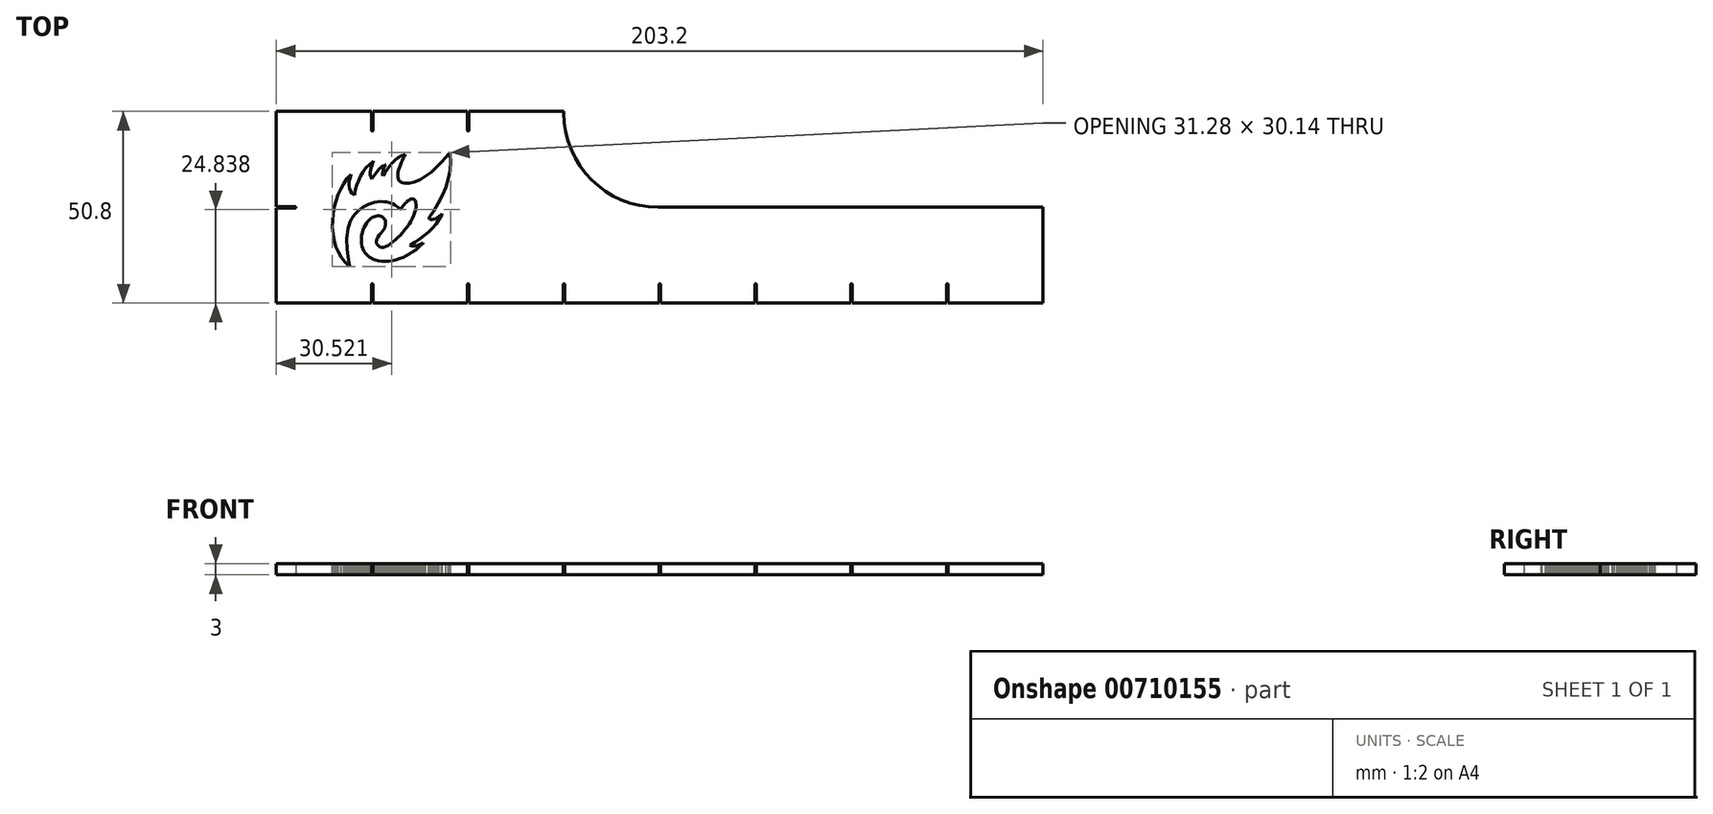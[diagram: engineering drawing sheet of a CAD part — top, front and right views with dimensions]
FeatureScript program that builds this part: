
annotation { "Feature Type Name" : "Feature", "Feature Type Description" : "" }
export const myFeature = defineFeature(function(context is Context, id is Id, definition is map)
    precondition{}
    {
        {
            var Q0;
            Q0=qCreatedBy(makeId("Top.planeOp"),FACE);
            var sketch = newSketch(context, id + "F0", { "sketchPlane" : qUnion([Q0])});
            skLineSegment(sketch, "E0", {"start": v(-76.2, 0) * mm, "end": v(127, 0) * mm});
            skLineSegment(sketch, "E1", {"start": v(127, 0) * mm, "end": v(127, 25.4) * mm});
            skLineSegment(sketch, "E2", {"start": v(127, 25.4) * mm, "end": v(0, 25.4) * mm});
            skLineSegment(sketch, "E3", {"start": v(0, 25.4) * mm, "end": v(0, 50.8) * mm});
            skLineSegment(sketch, "E4", {"start": v(0, 50.8) * mm, "end": v(-76.2, 50.8) * mm});
            skLineSegment(sketch, "E5", {"start": v(-76.2, 50.8) * mm, "end": v(-76.2, 0) * mm});
            skLineSegment(sketch, "E6", {"start": v(-76.2, 25.4) * mm, "end": v(-71.2, 25.4) * mm, "construction": true});
            skLineSegment(sketch, "E7", {"start": v(-50.8, 0) * mm, "end": v(-50.8, 5) * mm, "construction": true});
            skLineSegment(sketch, "E8", {"start": v(-50.8, 50.8) * mm, "end": v(-50.8, 45.8) * mm, "construction": true});
            skLineSegment(sketch, "E9.1.0.0", {"start": v(-25.4, 50.8) * mm, "end": v(-25.4, 45.8) * mm, "construction": true});
            skLineSegment(sketch, "E9.direction1", {"start": v(-50.8, 45.8) * mm, "end": v(-25.4, 45.8) * mm, "construction": true});
            skLineSegment(sketch, "E10.1.0.0", {"start": v(-25.4, 0) * mm, "end": v(-25.4, 5) * mm, "construction": true});
            skLineSegment(sketch, "E10.2.0.0", {"start": v(0, 0) * mm, "end": v(0, 5) * mm, "construction": true});
            skLineSegment(sketch, "E10.3.0.0", {"start": v(25.4, 0) * mm, "end": v(25.4, 5) * mm, "construction": true});
            skLineSegment(sketch, "E10.4.0.0", {"start": v(50.8, 0) * mm, "end": v(50.8, 5) * mm, "construction": true});
            skLineSegment(sketch, "E10.direction1", {"start": v(-50.8, 0) * mm, "end": v(-25.4, 0) * mm, "construction": true});
            skArc(sketch, "E11.0.startCap", {"start": v(-76.2, 25.2) * mm, "mid": v(-76.4, 25.4) * mm, "end": v(-76.2, 25.6) * mm});
            skArc(sketch, "E11.0.endCap", {"start": v(-71.2, 25.6) * mm, "mid": v(-71, 25.4) * mm, "end": v(-71.2, 25.2) * mm});
            skLineSegment(sketch, "E11.0.left", {"start": v(-76.2, 25.6) * mm, "end": v(-71.2, 25.6) * mm});
            skLineSegment(sketch, "E11.0.right", {"start": v(-76.2, 25.2) * mm, "end": v(-71.2, 25.2) * mm});
            skArc(sketch, "E11.1.startCap", {"start": v(-51, 50.8) * mm, "mid": v(-50.8, 51) * mm, "end": v(-50.6, 50.8) * mm});
            skArc(sketch, "E11.1.endCap", {"start": v(-50.6, 45.8) * mm, "mid": v(-50.8, 45.6) * mm, "end": v(-51, 45.8) * mm});
            skLineSegment(sketch, "E11.1.left", {"start": v(-50.6, 50.8) * mm, "end": v(-50.6, 45.8) * mm});
            skLineSegment(sketch, "E11.1.right", {"start": v(-51, 50.8) * mm, "end": v(-51, 45.8) * mm});
            skArc(sketch, "E11.2.startCap", {"start": v(-25.6, 50.8) * mm, "mid": v(-25.4, 51) * mm, "end": v(-25.2, 50.8) * mm});
            skArc(sketch, "E11.2.endCap", {"start": v(-25.2, 45.8) * mm, "mid": v(-25.4, 45.6) * mm, "end": v(-25.6, 45.8) * mm});
            skLineSegment(sketch, "E11.2.left", {"start": v(-25.2, 50.8) * mm, "end": v(-25.2, 45.8) * mm});
            skLineSegment(sketch, "E11.2.right", {"start": v(-25.6, 50.8) * mm, "end": v(-25.6, 45.8) * mm});
            skArc(sketch, "E11.3.startCap", {"start": v(-50.6, 0) * mm, "mid": v(-50.8, -0.2) * mm, "end": v(-51, 0) * mm});
            skArc(sketch, "E11.3.endCap", {"start": v(-51, 5) * mm, "mid": v(-50.8, 5.2) * mm, "end": v(-50.6, 5) * mm});
            skLineSegment(sketch, "E11.3.left", {"start": v(-51, 0) * mm, "end": v(-51, 5) * mm});
            skLineSegment(sketch, "E11.3.right", {"start": v(-50.6, 0) * mm, "end": v(-50.6, 5) * mm});
            skArc(sketch, "E11.4.startCap", {"start": v(-25.2, 0) * mm, "mid": v(-25.4, -0.2) * mm, "end": v(-25.6, 0) * mm});
            skArc(sketch, "E11.4.endCap", {"start": v(-25.6, 5) * mm, "mid": v(-25.4, 5.2) * mm, "end": v(-25.2, 5) * mm});
            skLineSegment(sketch, "E11.4.left", {"start": v(-25.6, 0) * mm, "end": v(-25.6, 5) * mm});
            skLineSegment(sketch, "E11.4.right", {"start": v(-25.2, 0) * mm, "end": v(-25.2, 5) * mm});
            skArc(sketch, "E11.5.startCap", {"start": v(0.2, 0) * mm, "mid": v(0, -0.2) * mm, "end": v(-0.2, 0) * mm});
            skArc(sketch, "E11.5.endCap", {"start": v(-0.2, 5) * mm, "mid": v(0, 5.2) * mm, "end": v(0.2, 5) * mm});
            skLineSegment(sketch, "E11.5.left", {"start": v(-0.2, 0) * mm, "end": v(-0.2, 5) * mm});
            skLineSegment(sketch, "E11.5.right", {"start": v(0.2, 0) * mm, "end": v(0.2, 5) * mm});
            skArc(sketch, "E11.6.startCap", {"start": v(25.6, 0) * mm, "mid": v(25.4, -0.2) * mm, "end": v(25.2, 0) * mm});
            skArc(sketch, "E11.6.endCap", {"start": v(25.2, 5) * mm, "mid": v(25.4, 5.2) * mm, "end": v(25.6, 5) * mm});
            skLineSegment(sketch, "E11.6.left", {"start": v(25.2, 0) * mm, "end": v(25.2, 5) * mm});
            skLineSegment(sketch, "E11.6.right", {"start": v(25.6, 0) * mm, "end": v(25.6, 5) * mm});
            skArc(sketch, "E11.7.startCap", {"start": v(51, 0) * mm, "mid": v(50.8, -0.2) * mm, "end": v(50.6, 0) * mm});
            skArc(sketch, "E11.7.endCap", {"start": v(50.6, 5) * mm, "mid": v(50.8, 5.2) * mm, "end": v(51, 5) * mm});
            skLineSegment(sketch, "E11.7.left", {"start": v(50.6, 0) * mm, "end": v(50.6, 5) * mm});
            skLineSegment(sketch, "E11.7.right", {"start": v(51, 0) * mm, "end": v(51, 5) * mm});
            skLineSegment(sketch, "E12.0.5.0", {"start": v(76.2, 0) * mm, "end": v(76.2, 5) * mm, "construction": true});
            skLineSegment(sketch, "E12.0.6.0", {"start": v(101.6, 0) * mm, "end": v(101.6, 5) * mm, "construction": true});
            skArc(sketch, "E13.0.startCap", {"start": v(76.4, 0) * mm, "mid": v(76.2, -0.2) * mm, "end": v(76, 0) * mm});
            skArc(sketch, "E13.0.endCap", {"start": v(76, 5) * mm, "mid": v(76.2, 5.2) * mm, "end": v(76.4, 5) * mm});
            skLineSegment(sketch, "E13.0.left", {"start": v(76, 0) * mm, "end": v(76, 5) * mm});
            skLineSegment(sketch, "E13.0.right", {"start": v(76.4, 0) * mm, "end": v(76.4, 5) * mm});
            skArc(sketch, "E13.1.startCap", {"start": v(101.8, 0) * mm, "mid": v(101.6, -0.2) * mm, "end": v(101.4, 0) * mm});
            skArc(sketch, "E13.1.endCap", {"start": v(101.4, 5) * mm, "mid": v(101.6, 5.2) * mm, "end": v(101.8, 5) * mm});
            skLineSegment(sketch, "E13.1.left", {"start": v(101.4, 0) * mm, "end": v(101.4, 5) * mm});
            skLineSegment(sketch, "E13.1.right", {"start": v(101.8, 0) * mm, "end": v(101.8, 5) * mm});
            skSolve(sketch);
        }
        {
            var Q0;
            {var subQ28=sQuery(id+"F0.wireOp",EDGE,"E1");Q0=makeQuery(id+"F0.imprint","IMPRINT",FACE,{"disambiguationData":[TD([[makeQuery(id+"F0.imprint","IMPRINT",EDGE,{"derivedFrom":subQ28}),1.0]])]});}
            extrude(context, id + "F1", {"entities" : qUnion([Q0]), "endBound" : BoundingType.SYMMETRIC, "depth" : 3 * mm, "offsetDistance" : 25 * mm});
        }
        {
            var Q0;
            Q0=makeQuery(id+"F1.opExtrude","SWEPT_EDGE",EDGE,{"disambiguationData":[OSD([sQuery(id+"F0.wireOp",EDGE,"E2"),sQuery(id+"F0.wireOp",EDGE,"E3")])]});
            fillet(context, id + "F2", {"entities" : qUnion([Q0]), "radius" : 25 * mm, "tangentPropagation" : true, "allowEdgeOverflow" : false});
        }
        {
            var Q0;
            Q0=makeQuery(id+"F1.opExtrude","CAP_FACE",FACE,{"disambiguationData":[OSD([sQuery(id+"F0.wireOp",EDGE,"E0"),sQuery(id+"F0.wireOp",EDGE,"E1"),sQuery(id+"F0.wireOp",EDGE,"E2"),sQuery(id+"F0.wireOp",EDGE,"E3"),sQuery(id+"F0.wireOp",EDGE,"E4"),sQuery(id+"F0.wireOp",EDGE,"E5"),sQuery(id+"F0.wireOp",EDGE,"E11.0.endCap"),sQuery(id+"F0.wireOp",EDGE,"E11.0.left"),sQuery(id+"F0.wireOp",EDGE,"E11.0.right"),sQuery(id+"F0.wireOp",EDGE,"E11.1.endCap"),sQuery(id+"F0.wireOp",EDGE,"E11.1.left"),sQuery(id+"F0.wireOp",EDGE,"E11.1.right"),sQuery(id+"F0.wireOp",EDGE,"E11.2.endCap"),sQuery(id+"F0.wireOp",EDGE,"E11.2.left"),sQuery(id+"F0.wireOp",EDGE,"E11.2.right"),sQuery(id+"F0.wireOp",EDGE,"E11.3.endCap"),sQuery(id+"F0.wireOp",EDGE,"E11.3.left"),sQuery(id+"F0.wireOp",EDGE,"E11.3.right"),sQuery(id+"F0.wireOp",EDGE,"E11.4.endCap"),sQuery(id+"F0.wireOp",EDGE,"E11.4.left"),sQuery(id+"F0.wireOp",EDGE,"E11.4.right"),sQuery(id+"F0.wireOp",EDGE,"E11.5.endCap"),sQuery(id+"F0.wireOp",EDGE,"E11.5.left"),sQuery(id+"F0.wireOp",EDGE,"E11.5.right"),sQuery(id+"F0.wireOp",EDGE,"E11.6.endCap"),sQuery(id+"F0.wireOp",EDGE,"E11.6.left"),sQuery(id+"F0.wireOp",EDGE,"E11.6.right"),sQuery(id+"F0.wireOp",EDGE,"E11.7.endCap"),sQuery(id+"F0.wireOp",EDGE,"E11.7.left"),sQuery(id+"F0.wireOp",EDGE,"E11.7.right")])],"isStart":false});
            var sketch = newSketch(context, id + "F3", { "sketchPlane" : qUnion([Q0])});
            skLineSegment(sketch, "E14", {"start": v(-30.21, 39.9) * mm, "end": v(-30.13, 39.32) * mm});
            skLineSegment(sketch, "E15", {"start": v(-30.13, 39.32) * mm, "end": v(-30.04, 37.5) * mm});
            skLineSegment(sketch, "E16", {"start": v(-30.04, 37.5) * mm, "end": v(-30.2, 35.18) * mm});
            skLineSegment(sketch, "E17", {"start": v(-30.2, 35.18) * mm, "end": v(-30.63, 32.92) * mm});
            skLineSegment(sketch, "E18", {"start": v(-30.63, 32.92) * mm, "end": v(-31.3, 30.72) * mm});
            skLineSegment(sketch, "E19", {"start": v(-31.3, 30.72) * mm, "end": v(-32.2, 28.59) * mm});
            skLineSegment(sketch, "E20", {"start": v(-32.2, 28.59) * mm, "end": v(-33.27, 26.5) * mm});
            skLineSegment(sketch, "E21", {"start": v(-33.27, 26.5) * mm, "end": v(-34.47, 24.48) * mm});
            skLineSegment(sketch, "E22", {"start": v(-34.47, 24.48) * mm, "end": v(-35.44, 22.99) * mm});
            skLineSegment(sketch, "E23", {"start": v(-35.44, 22.99) * mm, "end": v(-35.77, 22.5) * mm});
            skLineSegment(sketch, "E24", {"start": v(-35.77, 22.5) * mm, "end": v(-35.7, 22.4) * mm});
            skLineSegment(sketch, "E25", {"start": v(-35.7, 22.4) * mm, "end": v(-35.38, 22.2) * mm});
            skLineSegment(sketch, "E26", {"start": v(-35.38, 22.2) * mm, "end": v(-34.93, 22.13) * mm});
            skLineSegment(sketch, "E27", {"start": v(-34.93, 22.13) * mm, "end": v(-34.45, 22.23) * mm});
            skLineSegment(sketch, "E28", {"start": v(-34.45, 22.23) * mm, "end": v(-33.96, 22.45) * mm});
            skLineSegment(sketch, "E29", {"start": v(-33.96, 22.45) * mm, "end": v(-33.47, 22.75) * mm});
            skLineSegment(sketch, "E30", {"start": v(-33.47, 22.75) * mm, "end": v(-33, 23.08) * mm});
            skLineSegment(sketch, "E31", {"start": v(-33, 23.08) * mm, "end": v(-32.59, 23.4) * mm});
            skLineSegment(sketch, "E32", {"start": v(-32.59, 23.4) * mm, "end": v(-32.32, 23.6) * mm});
            skLineSegment(sketch, "E33", {"start": v(-32.32, 23.6) * mm, "end": v(-32.23, 23.67) * mm});
            skLineSegment(sketch, "E34", {"start": v(-32.23, 23.67) * mm, "end": v(-32.41, 23.31) * mm});
            skLineSegment(sketch, "E35", {"start": v(-32.41, 23.31) * mm, "end": v(-33, 22.28) * mm});
            skLineSegment(sketch, "E36", {"start": v(-33, 22.28) * mm, "end": v(-33.87, 21.03) * mm});
            skLineSegment(sketch, "E37", {"start": v(-33.87, 21.03) * mm, "end": v(-34.81, 19.9) * mm});
            skLineSegment(sketch, "E38", {"start": v(-34.81, 19.9) * mm, "end": v(-35.84, 18.86) * mm});
            skLineSegment(sketch, "E39", {"start": v(-35.84, 18.86) * mm, "end": v(-36.95, 17.92) * mm});
            skLineSegment(sketch, "E40", {"start": v(-36.95, 17.92) * mm, "end": v(-38.14, 17.03) * mm});
            skLineSegment(sketch, "E41", {"start": v(-38.14, 17.03) * mm, "end": v(-39.41, 16.2) * mm});
            skLineSegment(sketch, "E42", {"start": v(-39.41, 16.2) * mm, "end": v(-40.42, 15.58) * mm});
            skLineSegment(sketch, "E43", {"start": v(-40.42, 15.58) * mm, "end": v(-40.76, 15.38) * mm});
            skLineSegment(sketch, "E44", {"start": v(-40.76, 15.38) * mm, "end": v(-40.66, 15.32) * mm});
            skLineSegment(sketch, "E45", {"start": v(-40.66, 15.32) * mm, "end": v(-40.32, 15.19) * mm});
            skLineSegment(sketch, "E46", {"start": v(-40.32, 15.19) * mm, "end": v(-39.86, 15.1) * mm});
            skLineSegment(sketch, "E47", {"start": v(-39.86, 15.1) * mm, "end": v(-39.41, 15.12) * mm});
            skLineSegment(sketch, "E48", {"start": v(-39.41, 15.12) * mm, "end": v(-38.96, 15.21) * mm});
            skLineSegment(sketch, "E49", {"start": v(-38.96, 15.21) * mm, "end": v(-38.52, 15.37) * mm});
            skLineSegment(sketch, "E50", {"start": v(-38.52, 15.37) * mm, "end": v(-38.09, 15.57) * mm});
            skLineSegment(sketch, "E51", {"start": v(-38.09, 15.57) * mm, "end": v(-37.67, 15.8) * mm});
            skLineSegment(sketch, "E52", {"start": v(-37.67, 15.8) * mm, "end": v(-37.36, 15.97) * mm});
            skLineSegment(sketch, "E53", {"start": v(-37.36, 15.97) * mm, "end": v(-37.26, 16.03) * mm});
            skLineSegment(sketch, "E54", {"start": v(-37.26, 16.03) * mm, "end": v(-37.4, 15.86) * mm});
            skLineSegment(sketch, "E55", {"start": v(-37.4, 15.86) * mm, "end": v(-37.84, 15.39) * mm});
            skLineSegment(sketch, "E56", {"start": v(-37.84, 15.39) * mm, "end": v(-38.49, 14.76) * mm});
            skLineSegment(sketch, "E57", {"start": v(-38.49, 14.76) * mm, "end": v(-39.2, 14.17) * mm});
            skLineSegment(sketch, "E58", {"start": v(-39.2, 14.17) * mm, "end": v(-39.99, 13.6) * mm});
            skLineSegment(sketch, "E59", {"start": v(-39.99, 13.6) * mm, "end": v(-40.82, 13.08) * mm});
            skLineSegment(sketch, "E60", {"start": v(-40.82, 13.08) * mm, "end": v(-41.7, 12.6) * mm});
            skLineSegment(sketch, "E61", {"start": v(-41.7, 12.6) * mm, "end": v(-42.6, 12.17) * mm});
            skLineSegment(sketch, "E62", {"start": v(-42.6, 12.17) * mm, "end": v(-43.53, 11.8) * mm});
            skLineSegment(sketch, "E63", {"start": v(-43.53, 11.8) * mm, "end": v(-44.48, 11.5) * mm});
            skLineSegment(sketch, "E64", {"start": v(-44.48, 11.5) * mm, "end": v(-45.45, 11.28) * mm});
            skLineSegment(sketch, "E65", {"start": v(-45.45, 11.28) * mm, "end": v(-46.41, 11.14) * mm});
            skLineSegment(sketch, "E66", {"start": v(-46.41, 11.14) * mm, "end": v(-47.37, 11.08) * mm});
            skLineSegment(sketch, "E67", {"start": v(-47.37, 11.08) * mm, "end": v(-48.31, 11.12) * mm});
            skLineSegment(sketch, "E68", {"start": v(-48.31, 11.12) * mm, "end": v(-49.24, 11.26) * mm});
            skLineSegment(sketch, "E69", {"start": v(-49.24, 11.26) * mm, "end": v(-50.13, 11.5) * mm});
            skLineSegment(sketch, "E70", {"start": v(-50.13, 11.5) * mm, "end": v(-50.77, 11.76) * mm});
            skLineSegment(sketch, "E71", {"start": v(-50.77, 11.76) * mm, "end": v(-50.98, 11.86) * mm});
            skLineSegment(sketch, "E72", {"start": v(-50.98, 11.86) * mm, "end": v(-51.14, 11.95) * mm});
            skLineSegment(sketch, "E73", {"start": v(-51.14, 11.95) * mm, "end": v(-51.61, 12.25) * mm});
            skLineSegment(sketch, "E74", {"start": v(-51.61, 12.25) * mm, "end": v(-52.15, 12.7) * mm});
            skLineSegment(sketch, "E75", {"start": v(-52.15, 12.7) * mm, "end": v(-52.6, 13.23) * mm});
            skLineSegment(sketch, "E76", {"start": v(-52.6, 13.23) * mm, "end": v(-52.98, 13.8) * mm});
            skLineSegment(sketch, "E77", {"start": v(-52.98, 13.8) * mm, "end": v(-53.26, 14.43) * mm});
            skLineSegment(sketch, "E78", {"start": v(-53.26, 14.43) * mm, "end": v(-53.47, 15.1) * mm});
            skLineSegment(sketch, "E79", {"start": v(-53.47, 15.1) * mm, "end": v(-53.6, 15.8) * mm});
            skLineSegment(sketch, "E80", {"start": v(-53.6, 15.8) * mm, "end": v(-53.66, 16.5) * mm});
            skLineSegment(sketch, "E81", {"start": v(-53.66, 16.5) * mm, "end": v(-53.65, 17.23) * mm});
            skLineSegment(sketch, "E82", {"start": v(-53.65, 17.23) * mm, "end": v(-53.57, 17.95) * mm});
            skLineSegment(sketch, "E83", {"start": v(-53.57, 17.95) * mm, "end": v(-53.43, 18.67) * mm});
            skLineSegment(sketch, "E84", {"start": v(-53.43, 18.67) * mm, "end": v(-53.22, 19.37) * mm});
            skLineSegment(sketch, "E85", {"start": v(-53.22, 19.37) * mm, "end": v(-52.96, 20.05) * mm});
            skLineSegment(sketch, "E86", {"start": v(-52.96, 20.05) * mm, "end": v(-52.65, 20.69) * mm});
            skLineSegment(sketch, "E87", {"start": v(-52.65, 20.69) * mm, "end": v(-52.28, 21.28) * mm});
            skLineSegment(sketch, "E88", {"start": v(-52.28, 21.28) * mm, "end": v(-51.98, 21.7) * mm});
            skLineSegment(sketch, "E89", {"start": v(-51.98, 21.7) * mm, "end": v(-51.87, 21.83) * mm});
            skLineSegment(sketch, "E90", {"start": v(-51.87, 21.83) * mm, "end": v(-51.78, 21.93) * mm});
            skLineSegment(sketch, "E91", {"start": v(-51.78, 21.93) * mm, "end": v(-51.5, 22.2) * mm});
            skLineSegment(sketch, "E92", {"start": v(-51.5, 22.2) * mm, "end": v(-51.1, 22.52) * mm});
            skLineSegment(sketch, "E93", {"start": v(-51.1, 22.52) * mm, "end": v(-50.68, 22.77) * mm});
            skLineSegment(sketch, "E94", {"start": v(-50.68, 22.77) * mm, "end": v(-50.25, 22.95) * mm});
            skLineSegment(sketch, "E95", {"start": v(-50.25, 22.95) * mm, "end": v(-49.8, 23.08) * mm});
            skLineSegment(sketch, "E96", {"start": v(-49.8, 23.08) * mm, "end": v(-49.37, 23.13) * mm});
            skLineSegment(sketch, "E97", {"start": v(-49.37, 23.13) * mm, "end": v(-48.96, 23.13) * mm});
            skLineSegment(sketch, "E98", {"start": v(-48.96, 23.13) * mm, "end": v(-48.56, 23.06) * mm});
            skLineSegment(sketch, "E99", {"start": v(-48.56, 23.06) * mm, "end": v(-48.2, 22.92) * mm});
            skLineSegment(sketch, "E100", {"start": v(-48.2, 22.92) * mm, "end": v(-47.88, 22.72) * mm});
            skLineSegment(sketch, "E101", {"start": v(-47.88, 22.72) * mm, "end": v(-47.62, 22.45) * mm});
            skLineSegment(sketch, "E102", {"start": v(-47.62, 22.45) * mm, "end": v(-47.42, 22.11) * mm});
            skLineSegment(sketch, "E103", {"start": v(-47.42, 22.11) * mm, "end": v(-47.28, 21.71) * mm});
            skLineSegment(sketch, "E104", {"start": v(-47.28, 21.71) * mm, "end": v(-47.23, 21.24) * mm});
            skLineSegment(sketch, "E105", {"start": v(-47.23, 21.24) * mm, "end": v(-47.27, 20.7) * mm});
            skLineSegment(sketch, "E106", {"start": v(-47.27, 20.7) * mm, "end": v(-47.37, 20.25) * mm});
            skLineSegment(sketch, "E107", {"start": v(-47.37, 20.25) * mm, "end": v(-47.4, 20.1) * mm});
            skLineSegment(sketch, "E108", {"start": v(-47.4, 20.1) * mm, "end": v(-47.45, 19.98) * mm});
            skLineSegment(sketch, "E109", {"start": v(-47.45, 19.98) * mm, "end": v(-47.64, 19.62) * mm});
            skLineSegment(sketch, "E110", {"start": v(-47.64, 19.62) * mm, "end": v(-48, 19.11) * mm});
            skLineSegment(sketch, "E111", {"start": v(-48, 19.11) * mm, "end": v(-48.44, 18.59) * mm});
            skLineSegment(sketch, "E112", {"start": v(-48.44, 18.59) * mm, "end": v(-48.88, 18.05) * mm});
            skLineSegment(sketch, "E113", {"start": v(-48.88, 18.05) * mm, "end": v(-49.28, 17.5) * mm});
            skLineSegment(sketch, "E114", {"start": v(-49.28, 17.5) * mm, "end": v(-49.57, 16.94) * mm});
            skLineSegment(sketch, "E115", {"start": v(-49.57, 16.94) * mm, "end": v(-49.69, 16.37) * mm});
            skLineSegment(sketch, "E116", {"start": v(-49.69, 16.37) * mm, "end": v(-49.63, 15.93) * mm});
            skLineSegment(sketch, "E117", {"start": v(-49.63, 15.93) * mm, "end": v(-49.57, 15.8) * mm});
            skLineSegment(sketch, "E118", {"start": v(-49.57, 15.8) * mm, "end": v(-49.5, 15.65) * mm});
            skLineSegment(sketch, "E119", {"start": v(-49.5, 15.65) * mm, "end": v(-49.23, 15.25) * mm});
            skLineSegment(sketch, "E120", {"start": v(-49.23, 15.25) * mm, "end": v(-48.8, 14.92) * mm});
            skLineSegment(sketch, "E121", {"start": v(-48.8, 14.92) * mm, "end": v(-48.31, 14.78) * mm});
            skLineSegment(sketch, "E122", {"start": v(-48.31, 14.78) * mm, "end": v(-47.76, 14.82) * mm});
            skLineSegment(sketch, "E123", {"start": v(-47.76, 14.82) * mm, "end": v(-47.15, 15.01) * mm});
            skLineSegment(sketch, "E124", {"start": v(-47.15, 15.01) * mm, "end": v(-46.52, 15.33) * mm});
            skLineSegment(sketch, "E125", {"start": v(-46.52, 15.33) * mm, "end": v(-45.87, 15.75) * mm});
            skLineSegment(sketch, "E126", {"start": v(-45.87, 15.75) * mm, "end": v(-45.2, 16.26) * mm});
            skLineSegment(sketch, "E127", {"start": v(-45.2, 16.26) * mm, "end": v(-44.56, 16.82) * mm});
            skLineSegment(sketch, "E128", {"start": v(-44.56, 16.82) * mm, "end": v(-43.93, 17.41) * mm});
            skLineSegment(sketch, "E129", {"start": v(-43.93, 17.41) * mm, "end": v(-43.34, 18.02) * mm});
            skLineSegment(sketch, "E130", {"start": v(-43.34, 18.02) * mm, "end": v(-42.8, 18.62) * mm});
            skLineSegment(sketch, "E131", {"start": v(-42.8, 18.62) * mm, "end": v(-42.3, 19.18) * mm});
            skLineSegment(sketch, "E132", {"start": v(-42.3, 19.18) * mm, "end": v(-41.9, 19.68) * mm});
            skLineSegment(sketch, "E133", {"start": v(-41.9, 19.68) * mm, "end": v(-41.57, 20.1) * mm});
            skLineSegment(sketch, "E134", {"start": v(-41.57, 20.1) * mm, "end": v(-41.4, 20.34) * mm});
            skLineSegment(sketch, "E135", {"start": v(-41.4, 20.34) * mm, "end": v(-41.35, 20.42) * mm});
            skLineSegment(sketch, "E136", {"start": v(-41.35, 20.42) * mm, "end": v(-41.26, 20.57) * mm});
            skLineSegment(sketch, "E137", {"start": v(-41.26, 20.57) * mm, "end": v(-41, 21.01) * mm});
            skLineSegment(sketch, "E138", {"start": v(-41, 21.01) * mm, "end": v(-40.6, 21.7) * mm});
            skLineSegment(sketch, "E139", {"start": v(-40.6, 21.7) * mm, "end": v(-40.21, 22.46) * mm});
            skLineSegment(sketch, "E140", {"start": v(-40.21, 22.46) * mm, "end": v(-39.85, 23.26) * mm});
            skLineSegment(sketch, "E141", {"start": v(-39.85, 23.26) * mm, "end": v(-39.54, 24.08) * mm});
            skLineSegment(sketch, "E142", {"start": v(-39.54, 24.08) * mm, "end": v(-39.3, 24.89) * mm});
            skLineSegment(sketch, "E143", {"start": v(-39.3, 24.89) * mm, "end": v(-39.19, 25.65) * mm});
            skLineSegment(sketch, "E144", {"start": v(-39.19, 25.65) * mm, "end": v(-39.18, 26.17) * mm});
            skLineSegment(sketch, "E145", {"start": v(-39.18, 26.17) * mm, "end": v(-39.2, 26.34) * mm});
            skLineSegment(sketch, "E146", {"start": v(-39.2, 26.34) * mm, "end": v(-39.22, 26.46) * mm});
            skLineSegment(sketch, "E147", {"start": v(-39.22, 26.46) * mm, "end": v(-39.3, 26.84) * mm});
            skLineSegment(sketch, "E148", {"start": v(-39.3, 26.84) * mm, "end": v(-39.46, 27.22) * mm});
            skLineSegment(sketch, "E149", {"start": v(-39.46, 27.22) * mm, "end": v(-39.66, 27.47) * mm});
            skLineSegment(sketch, "E150", {"start": v(-39.66, 27.47) * mm, "end": v(-39.9, 27.6) * mm});
            skLineSegment(sketch, "E151", {"start": v(-39.9, 27.6) * mm, "end": v(-40.16, 27.64) * mm});
            skLineSegment(sketch, "E152", {"start": v(-40.16, 27.64) * mm, "end": v(-40.44, 27.6) * mm});
            skLineSegment(sketch, "E153", {"start": v(-40.44, 27.6) * mm, "end": v(-40.75, 27.48) * mm});
            skLineSegment(sketch, "E154", {"start": v(-40.75, 27.48) * mm, "end": v(-41.06, 27.29) * mm});
            skLineSegment(sketch, "E155", {"start": v(-41.06, 27.29) * mm, "end": v(-41.39, 27.05) * mm});
            skLineSegment(sketch, "E156", {"start": v(-41.39, 27.05) * mm, "end": v(-41.71, 26.77) * mm});
            skLineSegment(sketch, "E157", {"start": v(-41.71, 26.77) * mm, "end": v(-42.03, 26.46) * mm});
            skLineSegment(sketch, "E158", {"start": v(-42.03, 26.46) * mm, "end": v(-42.33, 26.14) * mm});
            skLineSegment(sketch, "E159", {"start": v(-42.33, 26.14) * mm, "end": v(-42.62, 25.8) * mm});
            skLineSegment(sketch, "E160", {"start": v(-42.62, 25.8) * mm, "end": v(-42.88, 25.48) * mm});
            skLineSegment(sketch, "E161", {"start": v(-42.88, 25.48) * mm, "end": v(-43.1, 25.18) * mm});
            skLineSegment(sketch, "E162", {"start": v(-43.1, 25.18) * mm, "end": v(-43.26, 24.97) * mm});
            skLineSegment(sketch, "E163", {"start": v(-43.26, 24.97) * mm, "end": v(-43.3, 24.9) * mm});
            skLineSegment(sketch, "E164", {"start": v(-43.3, 24.9) * mm, "end": v(-43.46, 25.05) * mm});
            skLineSegment(sketch, "E165", {"start": v(-43.46, 25.05) * mm, "end": v(-43.97, 25.48) * mm});
            skLineSegment(sketch, "E166", {"start": v(-43.97, 25.48) * mm, "end": v(-44.68, 25.95) * mm});
            skLineSegment(sketch, "E167", {"start": v(-44.68, 25.95) * mm, "end": v(-45.42, 26.33) * mm});
            skLineSegment(sketch, "E168", {"start": v(-45.42, 26.33) * mm, "end": v(-46.18, 26.61) * mm});
            skLineSegment(sketch, "E169", {"start": v(-46.18, 26.61) * mm, "end": v(-46.97, 26.8) * mm});
            skLineSegment(sketch, "E170", {"start": v(-46.97, 26.8) * mm, "end": v(-47.77, 26.9) * mm});
            skLineSegment(sketch, "E171", {"start": v(-47.77, 26.9) * mm, "end": v(-48.57, 26.93) * mm});
            skLineSegment(sketch, "E172", {"start": v(-48.57, 26.93) * mm, "end": v(-49.38, 26.87) * mm});
            skLineSegment(sketch, "E173", {"start": v(-49.38, 26.87) * mm, "end": v(-50.18, 26.73) * mm});
            skLineSegment(sketch, "E174", {"start": v(-50.18, 26.73) * mm, "end": v(-50.98, 26.51) * mm});
            skLineSegment(sketch, "E175", {"start": v(-50.98, 26.51) * mm, "end": v(-51.75, 26.23) * mm});
            skLineSegment(sketch, "E176", {"start": v(-51.75, 26.23) * mm, "end": v(-52.5, 25.87) * mm});
            skLineSegment(sketch, "E177", {"start": v(-52.5, 25.87) * mm, "end": v(-53.23, 25.45) * mm});
            skLineSegment(sketch, "E178", {"start": v(-53.23, 25.45) * mm, "end": v(-53.92, 24.97) * mm});
            skLineSegment(sketch, "E179", {"start": v(-53.92, 24.97) * mm, "end": v(-54.57, 24.43) * mm});
            skLineSegment(sketch, "E180", {"start": v(-54.57, 24.43) * mm, "end": v(-55.02, 23.98) * mm});
            skLineSegment(sketch, "E181", {"start": v(-55.02, 23.98) * mm, "end": v(-55.17, 23.83) * mm});
            skLineSegment(sketch, "E182", {"start": v(-55.17, 23.83) * mm, "end": v(-55.32, 23.66) * mm});
            skLineSegment(sketch, "E183", {"start": v(-55.32, 23.66) * mm, "end": v(-55.76, 23.1) * mm});
            skLineSegment(sketch, "E184", {"start": v(-55.76, 23.1) * mm, "end": v(-56.25, 22.33) * mm});
            skLineSegment(sketch, "E185", {"start": v(-56.25, 22.33) * mm, "end": v(-56.65, 21.53) * mm});
            skLineSegment(sketch, "E186", {"start": v(-56.65, 21.53) * mm, "end": v(-56.96, 20.69) * mm});
            skLineSegment(sketch, "E187", {"start": v(-56.96, 20.69) * mm, "end": v(-57.2, 19.82) * mm});
            skLineSegment(sketch, "E188", {"start": v(-57.2, 19.82) * mm, "end": v(-57.36, 18.93) * mm});
            skLineSegment(sketch, "E189", {"start": v(-57.36, 18.93) * mm, "end": v(-57.47, 18.02) * mm});
            skLineSegment(sketch, "E190", {"start": v(-57.47, 18.02) * mm, "end": v(-57.51, 17.1) * mm});
            skLineSegment(sketch, "E191", {"start": v(-57.51, 17.1) * mm, "end": v(-57.5, 16.16) * mm});
            skLineSegment(sketch, "E192", {"start": v(-57.5, 16.16) * mm, "end": v(-57.47, 15.22) * mm});
            skLineSegment(sketch, "E193", {"start": v(-57.47, 15.22) * mm, "end": v(-57.4, 14.28) * mm});
            skLineSegment(sketch, "E194", {"start": v(-57.4, 14.28) * mm, "end": v(-57.29, 13.35) * mm});
            skLineSegment(sketch, "E195", {"start": v(-57.29, 13.35) * mm, "end": v(-57.17, 12.43) * mm});
            skLineSegment(sketch, "E196", {"start": v(-57.17, 12.43) * mm, "end": v(-57.04, 11.52) * mm});
            skLineSegment(sketch, "E197", {"start": v(-57.04, 11.52) * mm, "end": v(-56.9, 10.63) * mm});
            skLineSegment(sketch, "E198", {"start": v(-56.9, 10.63) * mm, "end": v(-56.8, 9.98) * mm});
            skLineSegment(sketch, "E199", {"start": v(-56.8, 9.98) * mm, "end": v(-56.77, 9.77) * mm});
            skLineSegment(sketch, "E200", {"start": v(-56.77, 9.77) * mm, "end": v(-57.09, 10.01) * mm});
            skLineSegment(sketch, "E201", {"start": v(-57.09, 10.01) * mm, "end": v(-57.97, 10.85) * mm});
            skLineSegment(sketch, "E202", {"start": v(-57.97, 10.85) * mm, "end": v(-58.97, 12.1) * mm});
            skLineSegment(sketch, "E203", {"start": v(-58.97, 12.1) * mm, "end": v(-59.79, 13.5) * mm});
            skLineSegment(sketch, "E204", {"start": v(-59.79, 13.5) * mm, "end": v(-60.43, 15.03) * mm});
            skLineSegment(sketch, "E205", {"start": v(-60.43, 15.03) * mm, "end": v(-60.89, 16.65) * mm});
            skLineSegment(sketch, "E206", {"start": v(-60.89, 16.65) * mm, "end": v(-61.18, 18.35) * mm});
            skLineSegment(sketch, "E207", {"start": v(-61.18, 18.35) * mm, "end": v(-61.32, 20.1) * mm});
            skLineSegment(sketch, "E208", {"start": v(-61.32, 20.1) * mm, "end": v(-61.3, 21.87) * mm});
            skLineSegment(sketch, "E209", {"start": v(-61.3, 21.87) * mm, "end": v(-61.13, 23.64) * mm});
            skLineSegment(sketch, "E210", {"start": v(-61.13, 23.64) * mm, "end": v(-60.82, 25.4) * mm});
            skLineSegment(sketch, "E211", {"start": v(-60.82, 25.4) * mm, "end": v(-60.38, 27.1) * mm});
            skLineSegment(sketch, "E212", {"start": v(-60.38, 27.1) * mm, "end": v(-59.8, 28.75) * mm});
            skLineSegment(sketch, "E213", {"start": v(-59.8, 28.75) * mm, "end": v(-59.11, 30.3) * mm});
            skLineSegment(sketch, "E214", {"start": v(-59.11, 30.3) * mm, "end": v(-58.3, 31.73) * mm});
            skLineSegment(sketch, "E215", {"start": v(-58.3, 31.73) * mm, "end": v(-57.4, 33.02) * mm});
            skLineSegment(sketch, "E216", {"start": v(-57.4, 33.02) * mm, "end": v(-56.64, 33.88) * mm});
            skLineSegment(sketch, "E217", {"start": v(-56.64, 33.88) * mm, "end": v(-56.37, 34.15) * mm});
            skLineSegment(sketch, "E218", {"start": v(-56.37, 34.15) * mm, "end": v(-56.43, 33.97) * mm});
            skLineSegment(sketch, "E219", {"start": v(-56.43, 33.97) * mm, "end": v(-56.6, 33.41) * mm});
            skLineSegment(sketch, "E220", {"start": v(-56.6, 33.41) * mm, "end": v(-56.78, 32.66) * mm});
            skLineSegment(sketch, "E221", {"start": v(-56.78, 32.66) * mm, "end": v(-56.9, 31.9) * mm});
            skLineSegment(sketch, "E222", {"start": v(-56.9, 31.9) * mm, "end": v(-56.92, 31.17) * mm});
            skLineSegment(sketch, "E223", {"start": v(-56.92, 31.17) * mm, "end": v(-56.82, 30.45) * mm});
            skLineSegment(sketch, "E224", {"start": v(-56.82, 30.45) * mm, "end": v(-56.57, 29.78) * mm});
            skLineSegment(sketch, "E225", {"start": v(-56.57, 29.78) * mm, "end": v(-56.14, 29.18) * mm});
            skLineSegment(sketch, "E226", {"start": v(-56.14, 29.18) * mm, "end": v(-55.68, 28.76) * mm});
            skLineSegment(sketch, "E227", {"start": v(-55.68, 28.76) * mm, "end": v(-55.5, 28.65) * mm});
            skLineSegment(sketch, "E228", {"start": v(-55.5, 28.65) * mm, "end": v(-55.45, 28.98) * mm});
            skLineSegment(sketch, "E229", {"start": v(-55.45, 28.98) * mm, "end": v(-55.24, 29.98) * mm});
            skLineSegment(sketch, "E230", {"start": v(-55.24, 29.98) * mm, "end": v(-54.9, 31.26) * mm});
            skLineSegment(sketch, "E231", {"start": v(-54.9, 31.26) * mm, "end": v(-54.45, 32.5) * mm});
            skLineSegment(sketch, "E232", {"start": v(-54.45, 32.5) * mm, "end": v(-53.9, 33.68) * mm});
            skLineSegment(sketch, "E233", {"start": v(-53.9, 33.68) * mm, "end": v(-53.24, 34.79) * mm});
            skLineSegment(sketch, "E234", {"start": v(-53.24, 34.79) * mm, "end": v(-52.45, 35.83) * mm});
            skLineSegment(sketch, "E235", {"start": v(-52.45, 35.83) * mm, "end": v(-51.53, 36.78) * mm});
            skLineSegment(sketch, "E236", {"start": v(-51.53, 36.78) * mm, "end": v(-50.75, 37.45) * mm});
            skLineSegment(sketch, "E237", {"start": v(-50.75, 37.45) * mm, "end": v(-50.47, 37.64) * mm});
            skLineSegment(sketch, "E238", {"start": v(-50.47, 37.64) * mm, "end": v(-50.52, 37.5) * mm});
            skLineSegment(sketch, "E239", {"start": v(-50.52, 37.5) * mm, "end": v(-50.66, 37.1) * mm});
            skLineSegment(sketch, "E240", {"start": v(-50.66, 37.1) * mm, "end": v(-50.87, 36.52) * mm});
            skLineSegment(sketch, "E241", {"start": v(-50.87, 36.52) * mm, "end": v(-51.06, 35.91) * mm});
            skLineSegment(sketch, "E242", {"start": v(-51.06, 35.91) * mm, "end": v(-51.22, 35.3) * mm});
            skLineSegment(sketch, "E243", {"start": v(-51.22, 35.3) * mm, "end": v(-51.3, 34.68) * mm});
            skLineSegment(sketch, "E244", {"start": v(-51.3, 34.68) * mm, "end": v(-51.29, 34.08) * mm});
            skLineSegment(sketch, "E245", {"start": v(-51.29, 34.08) * mm, "end": v(-51.15, 33.51) * mm});
            skLineSegment(sketch, "E246", {"start": v(-51.15, 33.51) * mm, "end": v(-50.96, 33.1) * mm});
            skLineSegment(sketch, "E247", {"start": v(-50.96, 33.1) * mm, "end": v(-50.87, 32.98) * mm});
            skLineSegment(sketch, "E248", {"start": v(-50.87, 32.98) * mm, "end": v(-50.78, 33.12) * mm});
            skLineSegment(sketch, "E249", {"start": v(-50.78, 33.12) * mm, "end": v(-50.5, 33.52) * mm});
            skLineSegment(sketch, "E250", {"start": v(-50.5, 33.52) * mm, "end": v(-50.13, 34.08) * mm});
            skLineSegment(sketch, "E251", {"start": v(-50.13, 34.08) * mm, "end": v(-49.75, 34.63) * mm});
            skLineSegment(sketch, "E252", {"start": v(-49.75, 34.63) * mm, "end": v(-49.34, 35.15) * mm});
            skLineSegment(sketch, "E253", {"start": v(-49.34, 35.15) * mm, "end": v(-48.89, 35.63) * mm});
            skLineSegment(sketch, "E254", {"start": v(-48.89, 35.63) * mm, "end": v(-48.4, 36.05) * mm});
            skLineSegment(sketch, "E255", {"start": v(-48.4, 36.05) * mm, "end": v(-47.84, 36.4) * mm});
            skLineSegment(sketch, "E256", {"start": v(-47.84, 36.4) * mm, "end": v(-47.38, 36.6) * mm});
            skLineSegment(sketch, "E257", {"start": v(-47.38, 36.6) * mm, "end": v(-47.22, 36.64) * mm});
            skLineSegment(sketch, "E258", {"start": v(-47.22, 36.64) * mm, "end": v(-47.33, 36.48) * mm});
            skLineSegment(sketch, "E259", {"start": v(-47.33, 36.48) * mm, "end": v(-47.64, 35.98) * mm});
            skLineSegment(sketch, "E260", {"start": v(-47.64, 35.98) * mm, "end": v(-47.94, 35.27) * mm});
            skLineSegment(sketch, "E261", {"start": v(-47.94, 35.27) * mm, "end": v(-48.07, 34.53) * mm});
            skLineSegment(sketch, "E262", {"start": v(-48.07, 34.53) * mm, "end": v(-48.03, 33.94) * mm});
            skLineSegment(sketch, "E263", {"start": v(-48.03, 33.94) * mm, "end": v(-47.97, 33.75) * mm});
            skLineSegment(sketch, "E264", {"start": v(-47.97, 33.75) * mm, "end": v(-47.81, 33.97) * mm});
            skLineSegment(sketch, "E265", {"start": v(-47.81, 33.97) * mm, "end": v(-47.35, 34.63) * mm});
            skLineSegment(sketch, "E266", {"start": v(-47.35, 34.63) * mm, "end": v(-46.73, 35.5) * mm});
            skLineSegment(sketch, "E267", {"start": v(-46.73, 35.5) * mm, "end": v(-46.1, 36.33) * mm});
            skLineSegment(sketch, "E268", {"start": v(-46.1, 36.33) * mm, "end": v(-45.45, 37.12) * mm});
            skLineSegment(sketch, "E269", {"start": v(-45.45, 37.12) * mm, "end": v(-44.74, 37.85) * mm});
            skLineSegment(sketch, "E270", {"start": v(-44.74, 37.85) * mm, "end": v(-43.95, 38.48) * mm});
            skLineSegment(sketch, "E271", {"start": v(-43.95, 38.48) * mm, "end": v(-43.05, 39.02) * mm});
            skLineSegment(sketch, "E272", {"start": v(-43.05, 39.02) * mm, "end": v(-42.28, 39.35) * mm});
            skLineSegment(sketch, "E273", {"start": v(-42.28, 39.35) * mm, "end": v(-42.02, 39.43) * mm});
            skLineSegment(sketch, "E274", {"start": v(-42.02, 39.43) * mm, "end": v(-42.08, 39.31) * mm});
            skLineSegment(sketch, "E275", {"start": v(-42.08, 39.31) * mm, "end": v(-42.26, 38.96) * mm});
            skLineSegment(sketch, "E276", {"start": v(-42.26, 38.96) * mm, "end": v(-42.54, 38.42) * mm});
            skLineSegment(sketch, "E277", {"start": v(-42.54, 38.42) * mm, "end": v(-42.82, 37.83) * mm});
            skLineSegment(sketch, "E278", {"start": v(-42.82, 37.83) * mm, "end": v(-43.1, 37.2) * mm});
            skLineSegment(sketch, "E279", {"start": v(-43.1, 37.2) * mm, "end": v(-43.37, 36.55) * mm});
            skLineSegment(sketch, "E280", {"start": v(-43.37, 36.55) * mm, "end": v(-43.6, 35.9) * mm});
            skLineSegment(sketch, "E281", {"start": v(-43.6, 35.9) * mm, "end": v(-43.8, 35.23) * mm});
            skLineSegment(sketch, "E282", {"start": v(-43.8, 35.23) * mm, "end": v(-43.94, 34.59) * mm});
            skLineSegment(sketch, "E283", {"start": v(-43.94, 34.59) * mm, "end": v(-44.01, 33.98) * mm});
            skLineSegment(sketch, "E284", {"start": v(-44.01, 33.98) * mm, "end": v(-44, 33.41) * mm});
            skLineSegment(sketch, "E285", {"start": v(-44, 33.41) * mm, "end": v(-43.88, 32.91) * mm});
            skLineSegment(sketch, "E286", {"start": v(-43.88, 32.91) * mm, "end": v(-43.66, 32.48) * mm});
            skLineSegment(sketch, "E287", {"start": v(-43.66, 32.48) * mm, "end": v(-43.31, 32.14) * mm});
            skLineSegment(sketch, "E288", {"start": v(-43.31, 32.14) * mm, "end": v(-42.83, 31.9) * mm});
            skLineSegment(sketch, "E289", {"start": v(-42.83, 31.9) * mm, "end": v(-42.19, 31.77) * mm});
            skLineSegment(sketch, "E290", {"start": v(-42.19, 31.77) * mm, "end": v(-41.58, 31.76) * mm});
            skLineSegment(sketch, "E291", {"start": v(-41.58, 31.76) * mm, "end": v(-41.38, 31.78) * mm});
            skLineSegment(sketch, "E292", {"start": v(-41.38, 31.78) * mm, "end": v(-40.97, 31.81) * mm});
            skLineSegment(sketch, "E293", {"start": v(-40.97, 31.81) * mm, "end": v(-39.74, 32.1) * mm});
            skLineSegment(sketch, "E294", {"start": v(-39.74, 32.1) * mm, "end": v(-38.15, 32.75) * mm});
            skLineSegment(sketch, "E295", {"start": v(-38.15, 32.75) * mm, "end": v(-36.6, 33.66) * mm});
            skLineSegment(sketch, "E296", {"start": v(-36.6, 33.66) * mm, "end": v(-35.14, 34.77) * mm});
            skLineSegment(sketch, "E297", {"start": v(-35.14, 34.77) * mm, "end": v(-33.75, 36.02) * mm});
            skLineSegment(sketch, "E298", {"start": v(-33.75, 36.02) * mm, "end": v(-32.46, 37.33) * mm});
            skLineSegment(sketch, "E299", {"start": v(-32.46, 37.33) * mm, "end": v(-31.27, 38.65) * mm});
            skLineSegment(sketch, "E300", {"start": v(-31.27, 38.65) * mm, "end": v(-30.47, 39.6) * mm});
            skLineSegment(sketch, "E301", {"start": v(-30.47, 39.6) * mm, "end": v(-30.21, 39.9) * mm});
            skSolve(sketch);
        }
        {
            var Q0;
            Q0 = qSketchRegion(id + "F3", true);
            extrude(context, id + "F4", {"entities" : qUnion([Q0]), "operationType" : NewBodyOperationType.REMOVE, "endBound" : BoundingType.UP_TO_NEXT, "oppositeDirection" : true, "depth" : 25 * mm, "offsetDistance" : 25 * mm});
        }
    });
